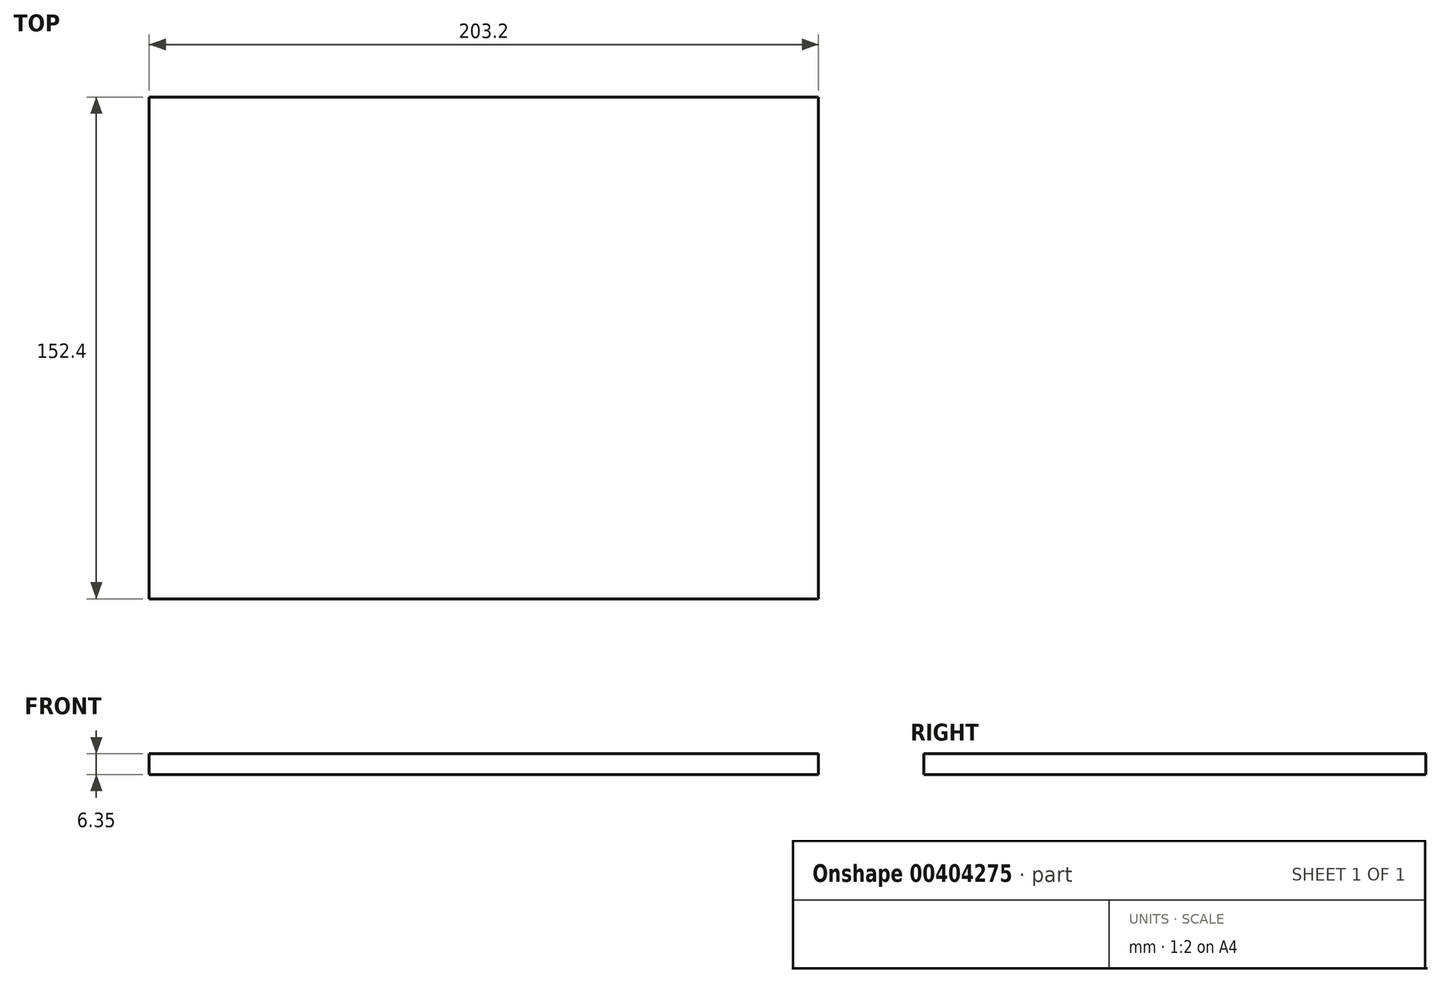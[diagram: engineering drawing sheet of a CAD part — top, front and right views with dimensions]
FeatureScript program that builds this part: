
annotation { "Feature Type Name" : "Feature", "Feature Type Description" : "" }
export const myFeature = defineFeature(function(context is Context, id is Id, definition is map)
    precondition{}
    {
        {
            var Q0;
            Q0=qCreatedBy(makeId("Top.planeOp"),FACE);
            var sketch = newSketch(context, id + "F0", { "sketchPlane" : qUnion([Q0])});
            skLineSegment(sketch, "E0.bottom", {"start": v(101.6, 76.2) * mm, "end": v(-101.6, 76.2) * mm});
            skLineSegment(sketch, "E0.top", {"start": v(101.6, -76.2) * mm, "end": v(-101.6, -76.2) * mm});
            skLineSegment(sketch, "E0.left", {"start": v(101.6, 76.2) * mm, "end": v(101.6, -76.2) * mm});
            skLineSegment(sketch, "E0.right", {"start": v(-101.6, 76.2) * mm, "end": v(-101.6, -76.2) * mm});
            skPoint(sketch, "E0.middle", {"position": v(0, 0) * mm});
            skSolve(sketch);
        }
        {
            var Q0;
            Q0 = qSketchRegion(id + "F0", true);
            extrude(context, id + "F1", {"entities" : qUnion([Q0]), "depth" : 6.35 * mm});
        }
    });
